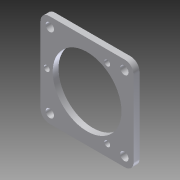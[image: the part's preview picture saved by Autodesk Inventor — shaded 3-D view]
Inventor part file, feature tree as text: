
AUTODESK INVENTOR PART (.ipt)
format: ipt  version: 2012 (Build 160160000, 160)  size: 162,816 bytes
history: native  units: in
note: dims shown in document units (in); Inventor stores cm internally (conversion verified against a paired STEP export)
features: extrude x2, fillet x2, sketch x1, hole x1
ambient origin geometry x8: Origin, YZ Plane, XZ Plane, XY Plane, X Axis, Y Axis, Z Axis, Center Point
bodies: Solid1 (feature_tree)
feature tree (6):
  sketch  "Sketch1"  dims[d0=0.9449in d1=0.4724in d2=1.0236in d3=0.5118in d4=0.0787in d5=0.2559in d6=0.128in d7=0.0787in d8=0.5625in d9=2.0in d10=1.0in d11=2.0in d12=1.0in d13=0.1181in d14=0.3937in d15=0.1575in d16=0.1575in d17=0.1575in d18=0.1575in d19=0.1575in d20=0.2in d21=0.2in d22=0.2in d23=0.2in d24=0.125in d25=0.0in d26=0.125in d27=0.18in d28=0.75in d29=0.27in d30=0.2in d31=0.5635in d32=1.0in d33=0.8108in d34=1.6in d35=1.6in d44=1.475in d45=0.125in d46=0.125in d47=0.125in d48=1.5in d50=1.5in d54=1.0in d55=0.0in d56=0.1875in d57=1.732in d58=1.4999in]
  extrude  "Extrusion1"  Depth=0.4724in
  fillet  "Fillet1"  Radius=1.0236in
  hole  "Hole1"  [1 undecoded]
  extrude  "Extrusion2"  Depth=0.0787in
  fillet  "Fillet2"  Radius=0.2559in
note: 1 required parameter value undecoded (feature->parameter linkage not recoverable at this tier; creation-order binding heuristic only, values carry confidence <= 0.55)
